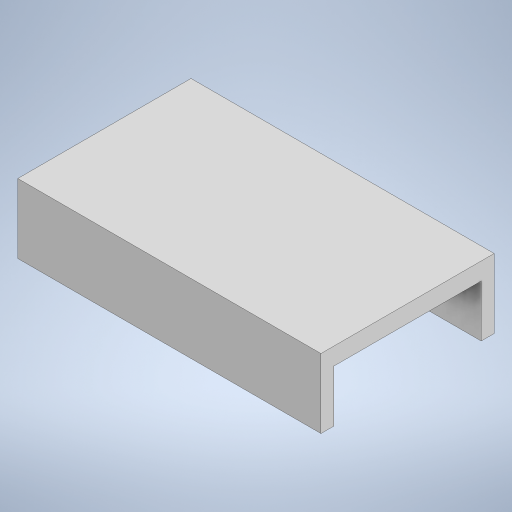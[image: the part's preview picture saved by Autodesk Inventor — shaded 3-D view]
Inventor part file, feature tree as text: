
AUTODESK INVENTOR PART (.ipt)
format: ipt  version: 2023 (Build 270158000, 158)  size: 209,920 bytes
history: native  units: mm
features: extrude x2, sketch x2, other x1
ambient origin geometry x8: Origin, YZ Plane, XZ Plane, XY Plane, X Axis, Y Axis, Z Axis, Center Point
bodies: Body1 (feature_tree)
feature tree (5):
  other  "Твердое тело1"
  extrude  "Выдавливание1"  Depth=40.0mm
  extrude  "Выдавливание2"  Depth=70.0mm
  sketch  "Эскиз1"
  sketch  "Эскиз2"
